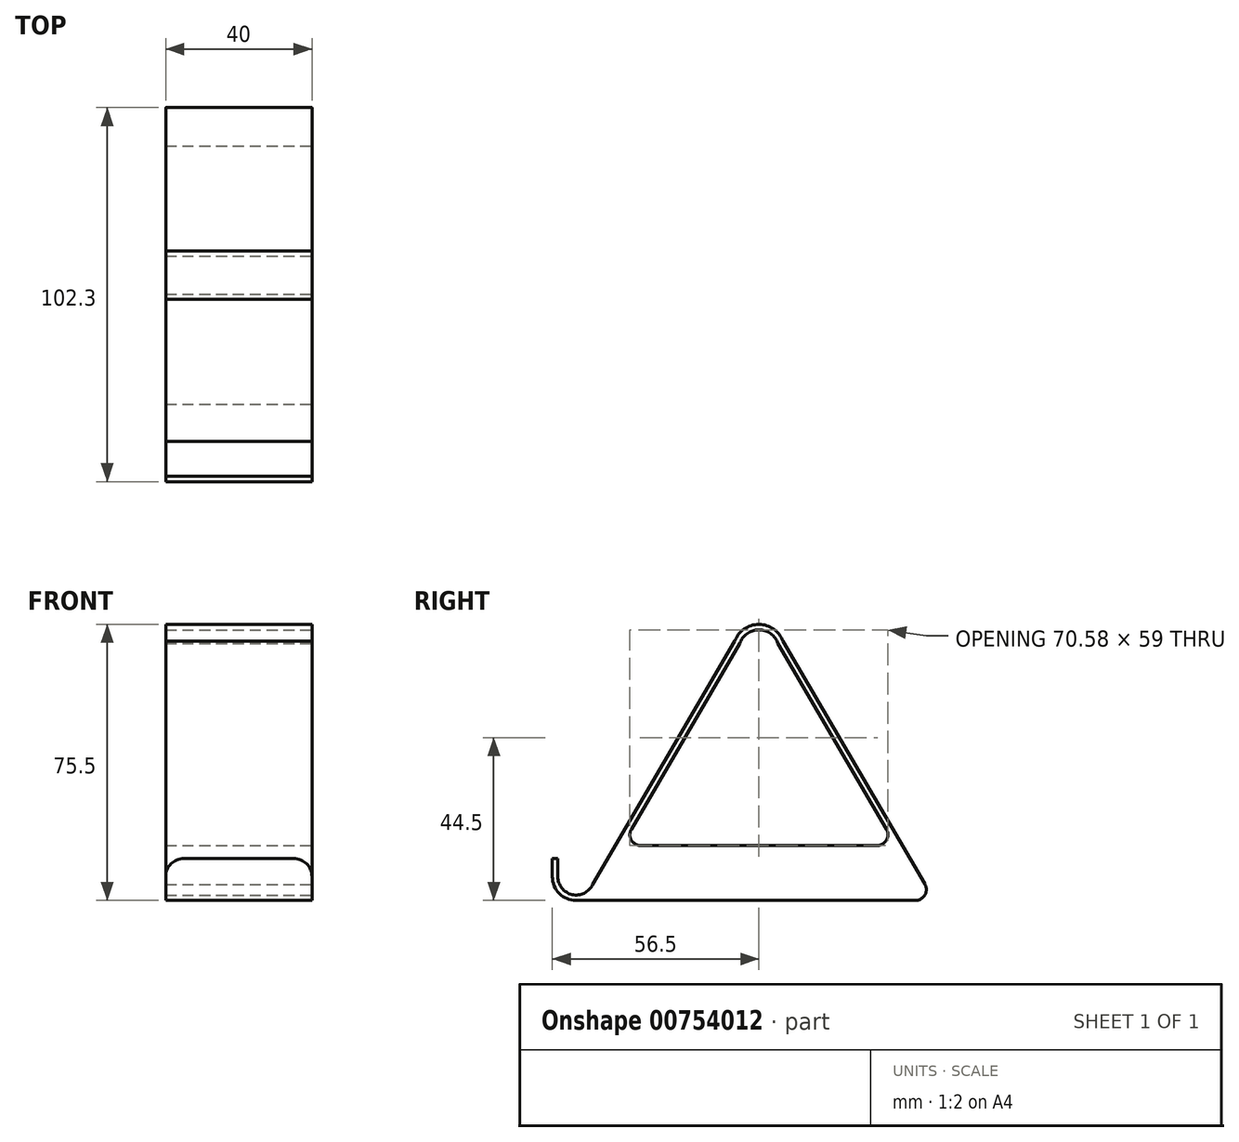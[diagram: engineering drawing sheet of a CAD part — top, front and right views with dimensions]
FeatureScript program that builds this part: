
annotation { "Feature Type Name" : "Feature", "Feature Type Description" : "" }
export const myFeature = defineFeature(function(context is Context, id is Id, definition is map)
    precondition{}
    {
        {
            var Q0;
            Q0=qCreatedBy(makeId("Right.planeOp"),FACE);
            var sketch = newSketch(context, id + "F0", { "sketchPlane" : qUnion([Q0])});
            skArc(sketch, "E0", {"start": v(-6.5, 0) * mm, "mid": v(-1.45, -6.34) * mm, "end": v(5.85, -2.83) * mm});
            skArc(sketch, "E1", {"start": v(55.22, 63.73) * mm, "mid": v(50, 67.5) * mm, "end": v(44.78, 63.73) * mm});
            skLineSegment(sketch, "E2", {"start": v(15.12, 13.01) * mm, "end": v(44.78, 63.73) * mm});
            skLineSegment(sketch, "E3", {"start": v(50, 62) * mm, "end": v(50, -38.41) * mm});
            skLineSegment(sketch, "E4.MirrorCS", {"start": v(84.88, 13.01) * mm, "end": v(55.22, 63.73) * mm});
            skLineSegment(sketch, "E5", {"start": v(0, -6.5) * mm, "end": v(92.8, -6.5) * mm});
            skPoint(sketch, "E6.orphan", {"position": v(94.15, -2.83) * mm});
            skLineSegment(sketch, "E7", {"start": v(-6.5, 0) * mm, "end": v(-6.5, 5) * mm});
            skLineSegment(sketch, "E8.0", {"start": v(-5, 0) * mm, "end": v(-5, 5) * mm});
            skLineSegment(sketch, "E8.1", {"start": v(95.4, -1.99) * mm, "end": v(56.59, 64.36) * mm});
            skArc(sketch, "E8.2", {"start": v(56.59, 64.36) * mm, "mid": v(50, 69) * mm, "end": v(43.41, 64.36) * mm});
            skLineSegment(sketch, "E8.3", {"start": v(4.52, -2.13) * mm, "end": v(43.41, 64.36) * mm});
            skArc(sketch, "E8.4", {"start": v(-5, 0) * mm, "mid": v(-1.1, -4.88) * mm, "end": v(4.52, -2.13) * mm});
            skLineSegment(sketch, "E9", {"start": v(-6.5, 5) * mm, "end": v(-5, 5) * mm});
            skLineSegment(sketch, "E10", {"start": v(0, -6.5) * mm, "end": v(98.03, -6.5) * mm});
            skLineSegment(sketch, "E11.0", {"start": v(17.7, 8.5) * mm, "end": v(82.3, 8.5) * mm});
            skPoint(sketch, "E12.newPointB", {"position": v(5.85, -2.83) * mm});
            skArc(sketch, "E12.filletArc", {"start": v(15.12, 13.01) * mm, "mid": v(15.1, 10) * mm, "end": v(17.7, 8.5) * mm});
            skArc(sketch, "E13.filletArc", {"start": v(82.3, 8.5) * mm, "mid": v(84.9, 10) * mm, "end": v(84.88, 13.01) * mm});
            skArc(sketch, "E14.filletArc", {"start": v(92.8, -6.5) * mm, "mid": v(95.4, -5) * mm, "end": v(95.4, -1.99) * mm});
            skSolve(sketch);
        }
        {
            var Q0;
            Q0=makeQuery(id+"F0.imprint","IMPRINT",FACE,{"disambiguationData":[TD([[makeQuery(id+"F0.imprint","IMPRINT",EDGE,{"derivedFrom":sQuery(id+"F0.wireOp",EDGE,"E1")}),-1.0]])]});
            extrude(context, id + "F1", {"entities" : qUnion([Q0]), "oppositeDirection" : true, "depth" : 40 * mm, "offsetDistance" : 25 * mm});
        }
        {
            var Q0;
            Q0=makeQuery(id+"F1.opExtrude","CAP_EDGE",EDGE,{"disambiguationData":[OSD([sQuery(id+"F0.wireOp",EDGE,"E9")])],"isStart":true});
            var Q1;
            Q1=makeQuery(id+"F1.opExtrude","CAP_EDGE",EDGE,{"disambiguationData":[OSD([sQuery(id+"F0.wireOp",EDGE,"E9")])],"isStart":false});
            fillet(context, id + "F2", {"entities" : qUnion([Q0, Q1]), "radius" : 5 * mm, "tangentPropagation" : true, "allowEdgeOverflow" : false});
        }
    });
